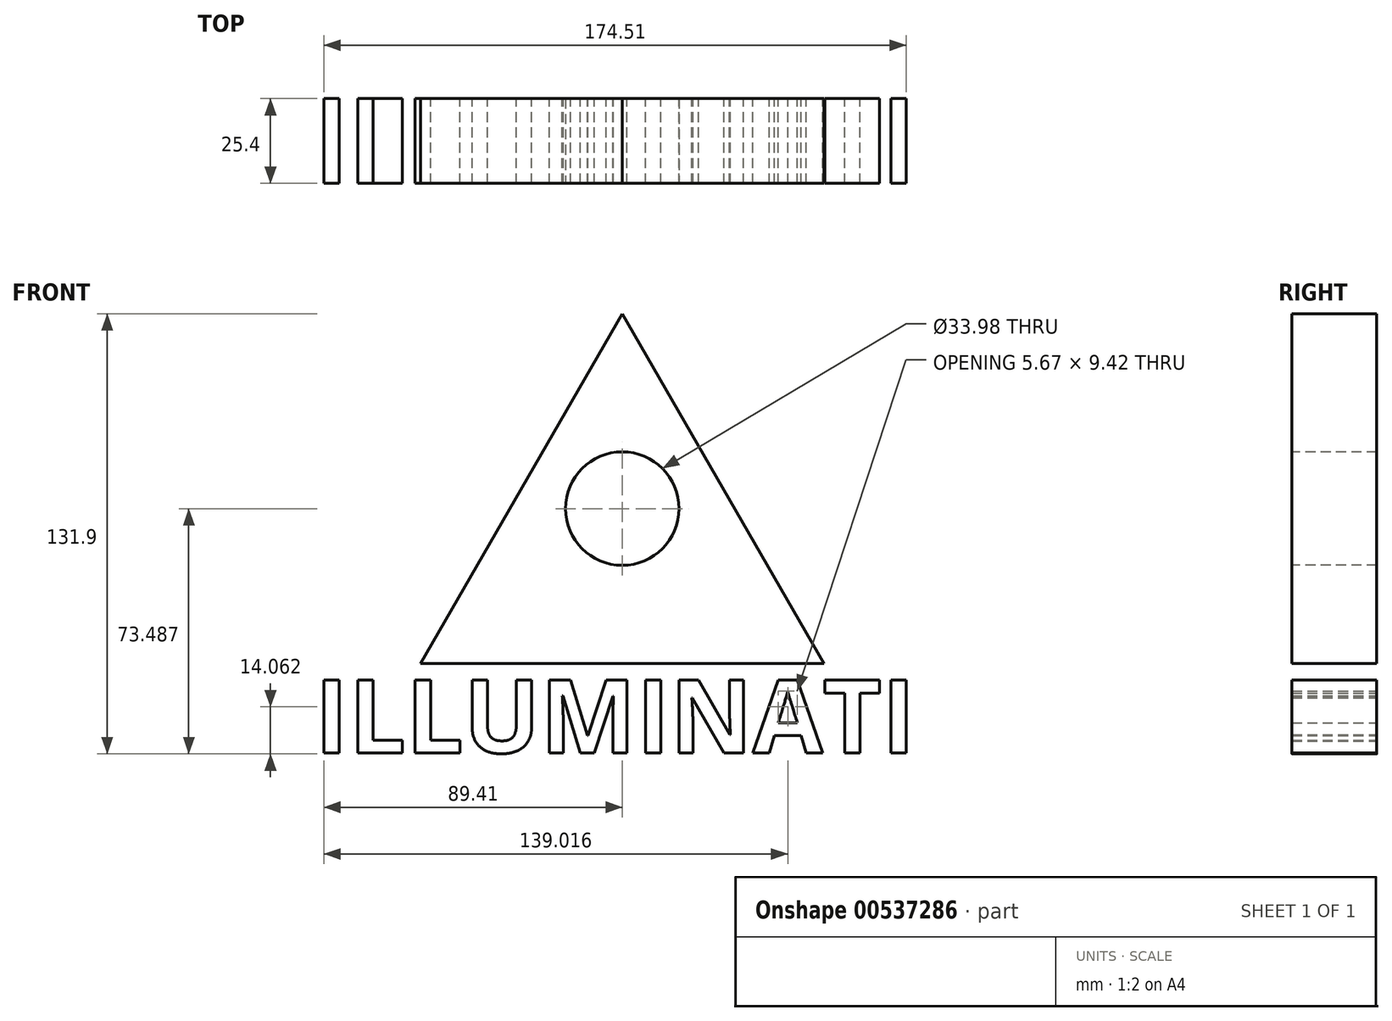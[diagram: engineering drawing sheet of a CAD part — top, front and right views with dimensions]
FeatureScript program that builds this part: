
annotation { "Feature Type Name" : "Feature", "Feature Type Description" : "" }
export const myFeature = defineFeature(function(context is Context, id is Id, definition is map)
    precondition{}
    {
        {
            var Q0;
            Q0=qCreatedBy(makeId("Front.planeOp"),FACE);
            var sketch = newSketch(context, id + "F0", { "sketchPlane" : qUnion([Q0])});
            skCircle(sketch, "E0.cCircle", {"center": v(0, 34.93) * mm, "radius": 34.93 * mm, "construction": true});
            skLineSegment(sketch, "E0.0", {"start": v(60.5, 0) * mm, "end": v(-60.5, 0) * mm});
            skLineSegment(sketch, "E0.1", {"start": v(-60.5, 0) * mm, "end": v(0, 104.78) * mm});
            skLineSegment(sketch, "E0.2", {"start": v(0, 104.78) * mm, "end": v(60.5, 0) * mm});
            skPoint(sketch, "E0.0.midPoint", {"position": v(0, 0) * mm});
            skSolve(sketch);
        }
        {
            var Q0;
            Q0 = qSketchRegion(id + "F0", true);
            extrude(context, id + "F1", {"entities" : qUnion([Q0]), "depth" : 25.4 * mm, "offsetDistance" : 25.4 * mm});
        }
        {
            var Q0;
            Q0=makeQuery(id+"F1.opExtrude","CAP_FACE",FACE,{"disambiguationData":[OSD([sQuery(id+"F0.wireOp",EDGE,"E0.0"),sQuery(id+"F0.wireOp",EDGE,"E0.1"),sQuery(id+"F0.wireOp",EDGE,"E0.2")])],"isStart":false});
            var sketch = newSketch(context, id + "F2", { "sketchPlane" : qUnion([Q0])});
            skCircle(sketch, "E1", {"center": v(0, 46.37) * mm, "radius": 17 * mm});
            skSolve(sketch);
        }
        {
            var Q0;
            Q0 = qSketchRegion(id + "F2", true);
            extrude(context, id + "F3", {"entities" : qUnion([Q0]), "operationType" : NewBodyOperationType.REMOVE, "endBound" : BoundingType.THROUGH_ALL, "oppositeDirection" : true, "depth" : 25.4 * mm, "offsetDistance" : 25.4 * mm});
        }
        {
            var Q0;
            Q0=qCreatedBy(makeId("Front.planeOp"),FACE);
            var sketch = newSketch(context, id + "F4", { "sketchPlane" : qUnion([Q0])});
            skText(sketch, "E2", { "text": "ILLUMINATI", "fontName": "OpenSans-Bold.ttf"});
            const initialGuessF4  = {"E2": [-0.09215, -0.02682, 1, 0, 0.02195]};
            skSetInitialGuess(sketch, initialGuessF4);
            skSolve(sketch);
        }
        {
            var Q0;
            Q0 = qSketchRegion(id + "F4", true);
            extrude(context, id + "F5", {"entities" : qUnion([Q0]), "depth" : 25.4 * mm, "offsetDistance" : 25.4 * mm});
        }
    });
